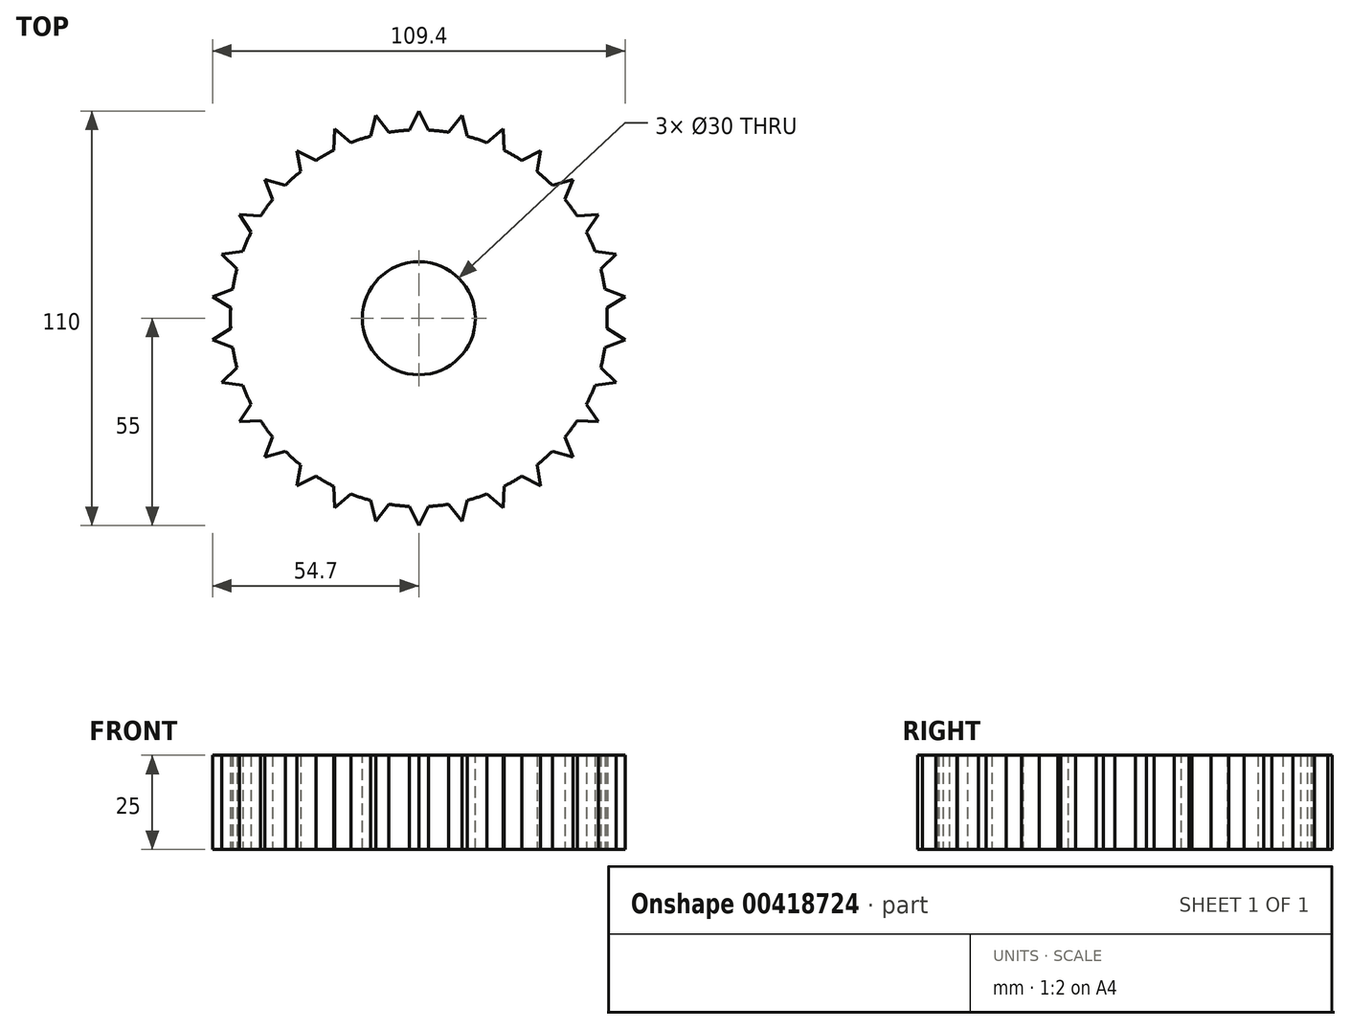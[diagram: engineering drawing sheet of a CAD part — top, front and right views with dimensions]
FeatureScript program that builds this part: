
annotation { "Feature Type Name" : "Feature", "Feature Type Description" : "" }
export const myFeature = defineFeature(function(context is Context, id is Id, definition is map)
    precondition{}
    {
        {
            var Q0;
            Q0=qCreatedBy(makeId("Top.planeOp"),FACE);
            var sketch = newSketch(context, id + "F0", { "sketchPlane" : qUnion([Q0])});
            skCircle(sketch, "E0", {"center": v(0, 0) * mm, "radius": 50 * mm});
            skPoint(sketch, "E1", {"position": v(0, 50) * mm});
            skLineSegment(sketch, "E2", {"start": v(0, 55) * mm, "end": v(0, 43.88) * mm, "construction": true});
            skLineSegment(sketch, "E3", {"start": v(0, 55) * mm, "end": v(-2.5, 49.94) * mm});
            skLineSegment(sketch, "E4.MirrorCS", {"start": v(0, 55) * mm, "end": v(2.5, 49.94) * mm});
            skLineSegment(sketch, "E5.1.0", {"start": v(-11.44, 53.8) * mm, "end": v(-12.83, 48.33) * mm});
            skLineSegment(sketch, "E5.1.1", {"start": v(-11.44, 53.8) * mm, "end": v(-7.94, 49.37) * mm});
            skLineSegment(sketch, "E5.2.0", {"start": v(-22.37, 50.25) * mm, "end": v(-22.6, 44.6) * mm});
            skLineSegment(sketch, "E5.2.1", {"start": v(-22.37, 50.25) * mm, "end": v(-18.03, 46.64) * mm});
            skLineSegment(sketch, "E5.3.0", {"start": v(-32.33, 44.5) * mm, "end": v(-31.38, 38.93) * mm});
            skLineSegment(sketch, "E5.3.1", {"start": v(-32.33, 44.5) * mm, "end": v(-27.33, 41.87) * mm});
            skLineSegment(sketch, "E5.4.0", {"start": v(-40.87, 36.8) * mm, "end": v(-38.78, 31.56) * mm});
            skLineSegment(sketch, "E5.4.1", {"start": v(-40.87, 36.8) * mm, "end": v(-35.44, 35.27) * mm});
            skLineSegment(sketch, "E5.5.0", {"start": v(-47.63, 27.5) * mm, "end": v(-44.5, 22.8) * mm});
            skLineSegment(sketch, "E5.5.1", {"start": v(-47.63, 27.5) * mm, "end": v(-42, 27.13) * mm});
            skLineSegment(sketch, "E5.6.0", {"start": v(-52.3, 17) * mm, "end": v(-48.27, 13.05) * mm});
            skLineSegment(sketch, "E5.6.1", {"start": v(-52.3, 17) * mm, "end": v(-46.72, 17.8) * mm});
            skLineSegment(sketch, "E5.7.0", {"start": v(-54.7, 5.75) * mm, "end": v(-49.93, 2.73) * mm});
            skLineSegment(sketch, "E5.7.1", {"start": v(-54.7, 5.75) * mm, "end": v(-49.4, 7.7) * mm});
            skLineSegment(sketch, "E5.8.0", {"start": v(-54.7, -5.75) * mm, "end": v(-49.4, -7.7) * mm});
            skLineSegment(sketch, "E5.8.1", {"start": v(-54.7, -5.75) * mm, "end": v(-49.93, -2.73) * mm});
            skLineSegment(sketch, "E5.9.0", {"start": v(-52.3, -17) * mm, "end": v(-46.72, -17.8) * mm});
            skLineSegment(sketch, "E5.9.1", {"start": v(-52.3, -17) * mm, "end": v(-48.27, -13.05) * mm});
            skLineSegment(sketch, "E5.10.0", {"start": v(-47.63, -27.5) * mm, "end": v(-42, -27.13) * mm});
            skLineSegment(sketch, "E5.10.1", {"start": v(-47.63, -27.5) * mm, "end": v(-44.5, -22.8) * mm});
            skLineSegment(sketch, "E5.11.0", {"start": v(-40.87, -36.8) * mm, "end": v(-35.44, -35.27) * mm});
            skLineSegment(sketch, "E5.11.1", {"start": v(-40.87, -36.8) * mm, "end": v(-38.78, -31.56) * mm});
            skLineSegment(sketch, "E5.12.0", {"start": v(-32.33, -44.5) * mm, "end": v(-27.33, -41.87) * mm});
            skLineSegment(sketch, "E5.12.1", {"start": v(-32.33, -44.5) * mm, "end": v(-31.38, -38.93) * mm});
            skLineSegment(sketch, "E5.13.0", {"start": v(-22.37, -50.25) * mm, "end": v(-18.03, -46.64) * mm});
            skLineSegment(sketch, "E5.13.1", {"start": v(-22.37, -50.25) * mm, "end": v(-22.6, -44.6) * mm});
            skLineSegment(sketch, "E5.14.0", {"start": v(-11.44, -53.8) * mm, "end": v(-7.94, -49.37) * mm});
            skLineSegment(sketch, "E5.14.1", {"start": v(-11.44, -53.8) * mm, "end": v(-12.83, -48.33) * mm});
            skLineSegment(sketch, "E5.15.0", {"start": v(0, -55) * mm, "end": v(2.5, -49.94) * mm});
            skLineSegment(sketch, "E5.15.1", {"start": v(0, -55) * mm, "end": v(-2.5, -49.94) * mm});
            skLineSegment(sketch, "E5.16.0", {"start": v(11.44, -53.8) * mm, "end": v(12.83, -48.33) * mm});
            skLineSegment(sketch, "E5.16.1", {"start": v(11.44, -53.8) * mm, "end": v(7.94, -49.37) * mm});
            skLineSegment(sketch, "E5.17.0", {"start": v(22.37, -50.25) * mm, "end": v(22.6, -44.6) * mm});
            skLineSegment(sketch, "E5.17.1", {"start": v(22.37, -50.25) * mm, "end": v(18.03, -46.64) * mm});
            skLineSegment(sketch, "E5.18.0", {"start": v(32.33, -44.5) * mm, "end": v(31.38, -38.93) * mm});
            skLineSegment(sketch, "E5.18.1", {"start": v(32.33, -44.5) * mm, "end": v(27.33, -41.87) * mm});
            skLineSegment(sketch, "E5.19.0", {"start": v(40.87, -36.8) * mm, "end": v(38.78, -31.56) * mm});
            skLineSegment(sketch, "E5.19.1", {"start": v(40.87, -36.8) * mm, "end": v(35.44, -35.27) * mm});
            skLineSegment(sketch, "E5.20.0", {"start": v(47.63, -27.5) * mm, "end": v(44.5, -22.8) * mm});
            skLineSegment(sketch, "E5.20.1", {"start": v(47.63, -27.5) * mm, "end": v(42, -27.13) * mm});
            skLineSegment(sketch, "E5.21.0", {"start": v(52.3, -17) * mm, "end": v(48.27, -13.05) * mm});
            skLineSegment(sketch, "E5.21.1", {"start": v(52.3, -17) * mm, "end": v(46.72, -17.8) * mm});
            skLineSegment(sketch, "E5.22.0", {"start": v(54.7, -5.75) * mm, "end": v(49.93, -2.73) * mm});
            skLineSegment(sketch, "E5.22.1", {"start": v(54.7, -5.75) * mm, "end": v(49.4, -7.7) * mm});
            skLineSegment(sketch, "E5.23.0", {"start": v(54.7, 5.75) * mm, "end": v(49.4, 7.7) * mm});
            skLineSegment(sketch, "E5.23.1", {"start": v(54.7, 5.75) * mm, "end": v(49.93, 2.73) * mm});
            skLineSegment(sketch, "E5.24.0", {"start": v(52.3, 17) * mm, "end": v(46.72, 17.8) * mm});
            skLineSegment(sketch, "E5.24.1", {"start": v(52.3, 17) * mm, "end": v(48.27, 13.05) * mm});
            skLineSegment(sketch, "E5.25.0", {"start": v(47.63, 27.5) * mm, "end": v(42, 27.13) * mm});
            skLineSegment(sketch, "E5.25.1", {"start": v(47.63, 27.5) * mm, "end": v(44.5, 22.8) * mm});
            skLineSegment(sketch, "E5.26.0", {"start": v(40.87, 36.8) * mm, "end": v(35.44, 35.27) * mm});
            skLineSegment(sketch, "E5.26.1", {"start": v(40.87, 36.8) * mm, "end": v(38.78, 31.56) * mm});
            skLineSegment(sketch, "E5.27.0", {"start": v(32.33, 44.5) * mm, "end": v(27.33, 41.87) * mm});
            skLineSegment(sketch, "E5.27.1", {"start": v(32.33, 44.5) * mm, "end": v(31.38, 38.93) * mm});
            skLineSegment(sketch, "E5.28.0", {"start": v(22.37, 50.25) * mm, "end": v(18.03, 46.64) * mm});
            skLineSegment(sketch, "E5.28.1", {"start": v(22.37, 50.25) * mm, "end": v(22.6, 44.6) * mm});
            skLineSegment(sketch, "E5.29.0", {"start": v(11.44, 53.8) * mm, "end": v(7.94, 49.37) * mm});
            skLineSegment(sketch, "E5.29.1", {"start": v(11.44, 53.8) * mm, "end": v(12.83, 48.33) * mm});
            skSolve(sketch);
        }
        {
            var Q0;
            Q0 = qSketchRegion(id + "F0", true);
            extrude(context, id + "F1", {"entities" : qUnion([Q0]), "depth" : 25 * mm});
        }
        {
            var Q0;
            Q0=makeQuery(id+"F1.opExtrude","CAP_FACE",FACE,{"disambiguationData":[OSD([sQuery(id+"F0.wireOp",EDGE,"E0"),sQuery(id+"F0.wireOp",EDGE,"E3"),sQuery(id+"F0.wireOp",EDGE,"E4.MirrorCS"),sQuery(id+"F0.wireOp",EDGE,"E5.1.0"),sQuery(id+"F0.wireOp",EDGE,"E5.1.1"),sQuery(id+"F0.wireOp",EDGE,"E5.2.0"),sQuery(id+"F0.wireOp",EDGE,"E5.2.1"),sQuery(id+"F0.wireOp",EDGE,"E5.3.0"),sQuery(id+"F0.wireOp",EDGE,"E5.3.1"),sQuery(id+"F0.wireOp",EDGE,"E5.4.0"),sQuery(id+"F0.wireOp",EDGE,"E5.4.1"),sQuery(id+"F0.wireOp",EDGE,"E5.5.0"),sQuery(id+"F0.wireOp",EDGE,"E5.5.1"),sQuery(id+"F0.wireOp",EDGE,"E5.6.0"),sQuery(id+"F0.wireOp",EDGE,"E5.6.1"),sQuery(id+"F0.wireOp",EDGE,"E5.7.0"),sQuery(id+"F0.wireOp",EDGE,"E5.7.1"),sQuery(id+"F0.wireOp",EDGE,"E5.8.0"),sQuery(id+"F0.wireOp",EDGE,"E5.8.1"),sQuery(id+"F0.wireOp",EDGE,"E5.9.0"),sQuery(id+"F0.wireOp",EDGE,"E5.9.1"),sQuery(id+"F0.wireOp",EDGE,"E5.10.0"),sQuery(id+"F0.wireOp",EDGE,"E5.10.1"),sQuery(id+"F0.wireOp",EDGE,"E5.11.0"),sQuery(id+"F0.wireOp",EDGE,"E5.11.1"),sQuery(id+"F0.wireOp",EDGE,"E5.12.0"),sQuery(id+"F0.wireOp",EDGE,"E5.12.1"),sQuery(id+"F0.wireOp",EDGE,"E5.13.0"),sQuery(id+"F0.wireOp",EDGE,"E5.13.1"),sQuery(id+"F0.wireOp",EDGE,"E5.14.0"),sQuery(id+"F0.wireOp",EDGE,"E5.14.1"),sQuery(id+"F0.wireOp",EDGE,"E5.15.0"),sQuery(id+"F0.wireOp",EDGE,"E5.15.1"),sQuery(id+"F0.wireOp",EDGE,"E5.16.0"),sQuery(id+"F0.wireOp",EDGE,"E5.16.1"),sQuery(id+"F0.wireOp",EDGE,"E5.17.0"),sQuery(id+"F0.wireOp",EDGE,"E5.17.1"),sQuery(id+"F0.wireOp",EDGE,"E5.18.0"),sQuery(id+"F0.wireOp",EDGE,"E5.18.1"),sQuery(id+"F0.wireOp",EDGE,"E5.19.0"),sQuery(id+"F0.wireOp",EDGE,"E5.19.1"),sQuery(id+"F0.wireOp",EDGE,"E5.20.0"),sQuery(id+"F0.wireOp",EDGE,"E5.20.1"),sQuery(id+"F0.wireOp",EDGE,"E5.21.0"),sQuery(id+"F0.wireOp",EDGE,"E5.21.1"),sQuery(id+"F0.wireOp",EDGE,"E5.22.0"),sQuery(id+"F0.wireOp",EDGE,"E5.22.1"),sQuery(id+"F0.wireOp",EDGE,"E5.23.0"),sQuery(id+"F0.wireOp",EDGE,"E5.23.1"),sQuery(id+"F0.wireOp",EDGE,"E5.24.0"),sQuery(id+"F0.wireOp",EDGE,"E5.24.1"),sQuery(id+"F0.wireOp",EDGE,"E5.25.0"),sQuery(id+"F0.wireOp",EDGE,"E5.25.1"),sQuery(id+"F0.wireOp",EDGE,"E5.26.0"),sQuery(id+"F0.wireOp",EDGE,"E5.26.1"),sQuery(id+"F0.wireOp",EDGE,"E5.27.0"),sQuery(id+"F0.wireOp",EDGE,"E5.27.1"),sQuery(id+"F0.wireOp",EDGE,"E5.28.0"),sQuery(id+"F0.wireOp",EDGE,"E5.28.1"),sQuery(id+"F0.wireOp",EDGE,"E5.29.0"),sQuery(id+"F0.wireOp",EDGE,"E5.29.1")])],"isStart":false});
            var sketch = newSketch(context, id + "F2", { "sketchPlane" : qUnion([Q0])});
            skCircle(sketch, "E6", {"center": v(0, 0) * mm, "radius": 15 * mm});
            skSolve(sketch);
        }
        {
            var Q0;
            Q0 = qSketchRegion(id + "F2", true);
            extrude(context, id + "F3", {"entities" : qUnion([Q0]), "operationType" : NewBodyOperationType.REMOVE, "oppositeDirection" : true, "depth" : 25 * mm});
        }
    });
